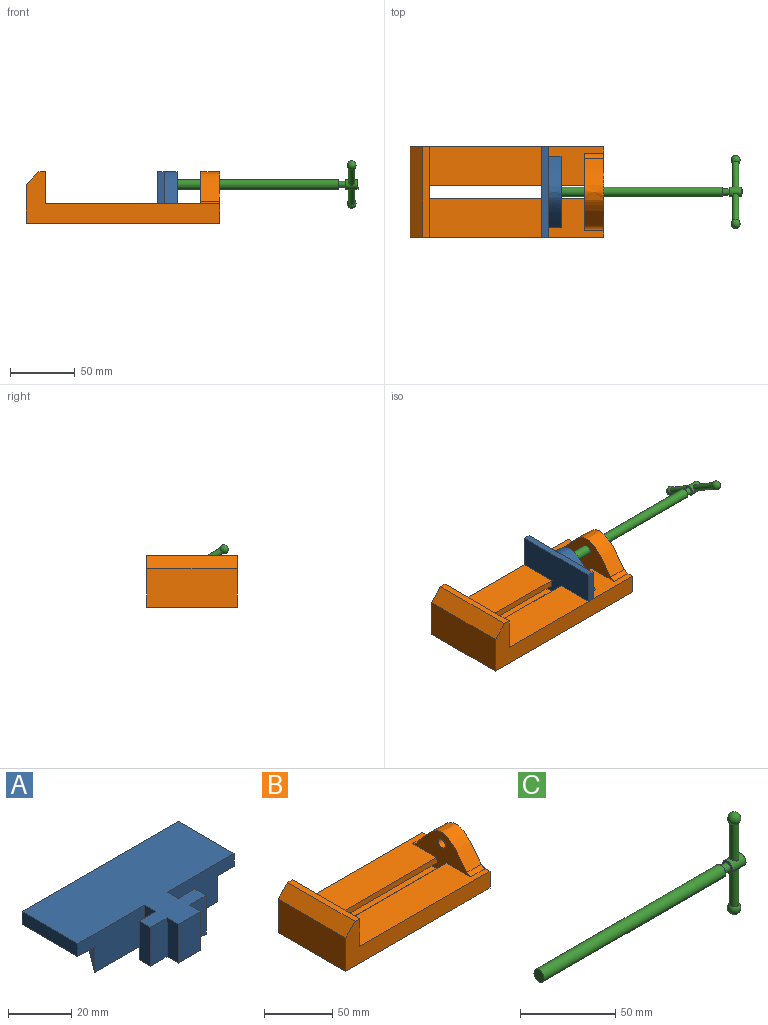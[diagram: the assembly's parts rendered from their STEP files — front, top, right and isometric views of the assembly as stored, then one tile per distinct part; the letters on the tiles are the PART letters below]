
ASSEMBLY  parts=3 mates=3
PART A: 23 faces, bbox 70x41.3x15 mm
  f0: cylinder r=3.75mm len=10mm, axis (0,0,-1), area 235.6mm2, adj f21,f22
  f1: plane 36.3x26.3mm, normal (0,0,-1), area 445.3mm2, adj f3,f4,f5,f20
  f2: plane 36.3x26.3mm, normal (0,0,-1), area 445.3mm2, adj f3,f17,f18,f20
  f3: plane 70x5mm, normal (0,1,0), area 350mm2, adj f1,f2,f4,f18,f19
  f4: plane 25x5mm, normal (-1,0,0), area 125mm2, adj f1,f3,f5,f19
  f5: plane 30x15mm, normal (0,-1,0), area 375mm2, adj f1,f4,f6,f19,f20,f21
  f6: plane 15x5mm, normal (-1,0,0), area 75mm2, adj f5,f7,f19,f21
  f7: plane 15x7.5mm, normal (0,1,0), area 112.5mm2, adj f6,f8,f19,f21
  f8: plane 15x5mm, normal (-1,0,0), area 75mm2, adj f7,f9,f19,f21
  f9: plane 15x7.5mm, normal (0,-1,0), area 112.5mm2, adj f8,f10,f19,f21
  f10: plane 15x5mm, normal (-1,0,0), area 75mm2, adj f9,f11,f19,f21
  f11: plane 15x10mm, normal (0,-1,0), area 150mm2, adj f10,f12,f19,f21
  f12: plane 15x5mm, normal (1,0,0), area 75mm2, adj f11,f13,f19,f21
  f13: plane 15x7.5mm, normal (0,-1,0), area 112.5mm2, adj f12,f14,f19,f21
  f14: plane 15x5mm, normal (1,0,0), area 75mm2, adj f13,f15,f19,f21
  f15: plane 15x7.5mm, normal (0,1,0), area 112.5mm2, adj f14,f16,f19,f21
  f16: plane 15x5mm, normal (1,0,0), area 75mm2, adj f15,f17,f19,f21
  f17: plane 30x15mm, normal (0,-1,0), area 375mm2, adj f2,f16,f18,f19,f20,f21
  f18: plane 25x5mm, normal (1,0,0), area 125mm2, adj f2,f3,f17,f19
  f19: plane 70x40mm, normal (0,0,1), area 1975mm2, adj f3,f4,f5,f6,f7,f8,f9,f10
  f20: extruded ~55x25mm, area 765.1mm2, adj f1,f2,f5,f17,f21
  f21: plane 55x41.3mm, normal (0,0,-1), area 1040.2mm2, adj f0,f5,f6,f7,f8,f9,f10,f11
  f22: plane 7.5x7.5mm, normal (0,0,-1), area 44.2mm2, adj f0
PART B: 25 faces, bbox 150x70x41.2 mm
  f0: plane 135x30mm, normal (0,0,1), area 3674.5mm2, adj f4,f5,f7,f14,f22,f23
  f1: plane 135x30mm, normal (0,0,1), area 3674.5mm2, adj f3,f4,f7,f15,f22,f24
  f2: plane 70x30mm, normal (-1,0,0), area 2100mm2, adj f3,f5,f6,f9
  f3: plane 150x40mm, normal (0,-1,0), area 2575mm2, adj f1,f2,f4,f6,f7,f8,f9
  f4: plane 70x41.18mm, normal (1,0,0), area 1867.1mm2, adj f0,f1,f3,f5,f6,f20,f21,f23
  f5: plane 150x40mm, normal (0,1,0), area 2575mm2, adj f0,f2,f4,f6,f7,f8,f9
  f6: plane 150x70mm, normal (0,0,-1), area 9300mm2, adj f2,f3,f4,f5,f7,f10,f19,f22
  f7: plane 70x40mm, normal (1,0,0), area 1975mm2, adj f0,f1,f3,f5,f6,f8,f10,f11
  f8: plane 70x5mm, normal (0,0,1), area 350mm2, adj f3,f5,f7,f9
  f9: plane 70x10mm, normal (-0.71,0,0.71), area 989.9mm2, adj f2,f3,f5,f8
  f10: plane 120x5mm, normal (0,-1,0), area 600mm2, adj f6,f7,f11,f22
  f11: plane 120x7.5mm, normal (0,0,1), area 900mm2, adj f7,f10,f12,f22
  f12: plane 120x5mm, normal (0,-1,0), area 600mm2, adj f7,f11,f13,f22
  f13: plane 120x7.5mm, normal (0,0,-1), area 900mm2, adj f7,f12,f14,f22
  f14: plane 120x5mm, normal (0,-1,0), area 600mm2, adj f0,f7,f13,f22
  f15: plane 120x5mm, normal (0,1,0), area 600mm2, adj f1,f7,f16,f22
  f16: plane 120x7.5mm, normal (0,0,-1), area 900mm2, adj f7,f15,f17,f22
  f17: plane 120x5mm, normal (0,1,0), area 600mm2, adj f7,f16,f18,f22
  f18: plane 120x7.5mm, normal (0,0,1), area 900mm2, adj f7,f17,f19,f22
  f19: plane 120x5mm, normal (0,1,0), area 600mm2, adj f6,f7,f18,f22
  f20: cylinder r=3.75mm len=15mm, axis (1,0,0), area 353.4mm2, adj f4,f22
  f21: extruded ~52.01x22.96mm, area 1071.8mm2, adj f4,f22,f23,f24
  f22: plane 60.06x41.18mm, normal (-1,0,0), area 1042.1mm2, adj f0,f1,f6,f10,f11,f12,f13,f14
  f23: cylinder r=5mm len=15mm, axis (1,0,0), area 70.2mm2, adj f0,f4,f21,f22
  f24: cylinder r=5mm len=15mm, axis (1,0,0), area 70.2mm2, adj f1,f4,f21,f22
PART C: 11 faces, bbox 150x7.5x64.5 mm
  f0: cylinder r=2.5mm len=23.51mm, axis (0,0,-1), area 361.4mm2, adj f8,f10
  f1: cylinder r=2.5mm len=23.51mm, axis (0,0,1), area 361.4mm2, adj f8,f9
  f2: cylinder r=2.5mm len=5mm, axis (-1,0,0), area 78.5mm2, adj f3,f6
  f3: plane 7.5x7.5mm, normal (1,0,0), area 24.5mm2, adj f2,f4
  f4: cylinder r=3.75mm len=135mm, axis (-1,0,0), area 3180.9mm2, adj f3,f5
  f5: plane 7.5x7.5mm, normal (-1,0,0), area 44.2mm2, adj f4
  f6: plane 7.5x7.5mm, normal (-1,0,0), area 24.5mm2, adj f2,f8
  f7: plane 7.5x7.5mm, normal (1,0,0), area 44.2mm2, adj f8
  f8: cylinder r=3.75mm len=10mm, axis (1,0,0), area 193.7mm2, adj f0,f1,f6,f7
  f9: sphere r=3.5mm, area 130.8mm2, adj f1
  f10: sphere r=3.5mm, area 130.8mm2, adj f0
PLACE A rot(axis=(0.58,-0.58,-0.58),120deg) t=(-43.18,35,27.5)mm
PLACE B t=(-75,35,0)mm
PLACE C rot(axis=(1,0,0),58.9deg) t=(31.82,33.39,30.97)mm
MATE slider A.f19 <-> B.f7  axis (1,0,0) through (-48.18,30,15)mm
MATE cylindrical C.f8 <-> B.f20  axis (1,0,0) through (91.82,35,30)mm
MATE pin_slot A.f0 <-> C.f2  axis (1,0,0) through (-43.18,35,30)mm
